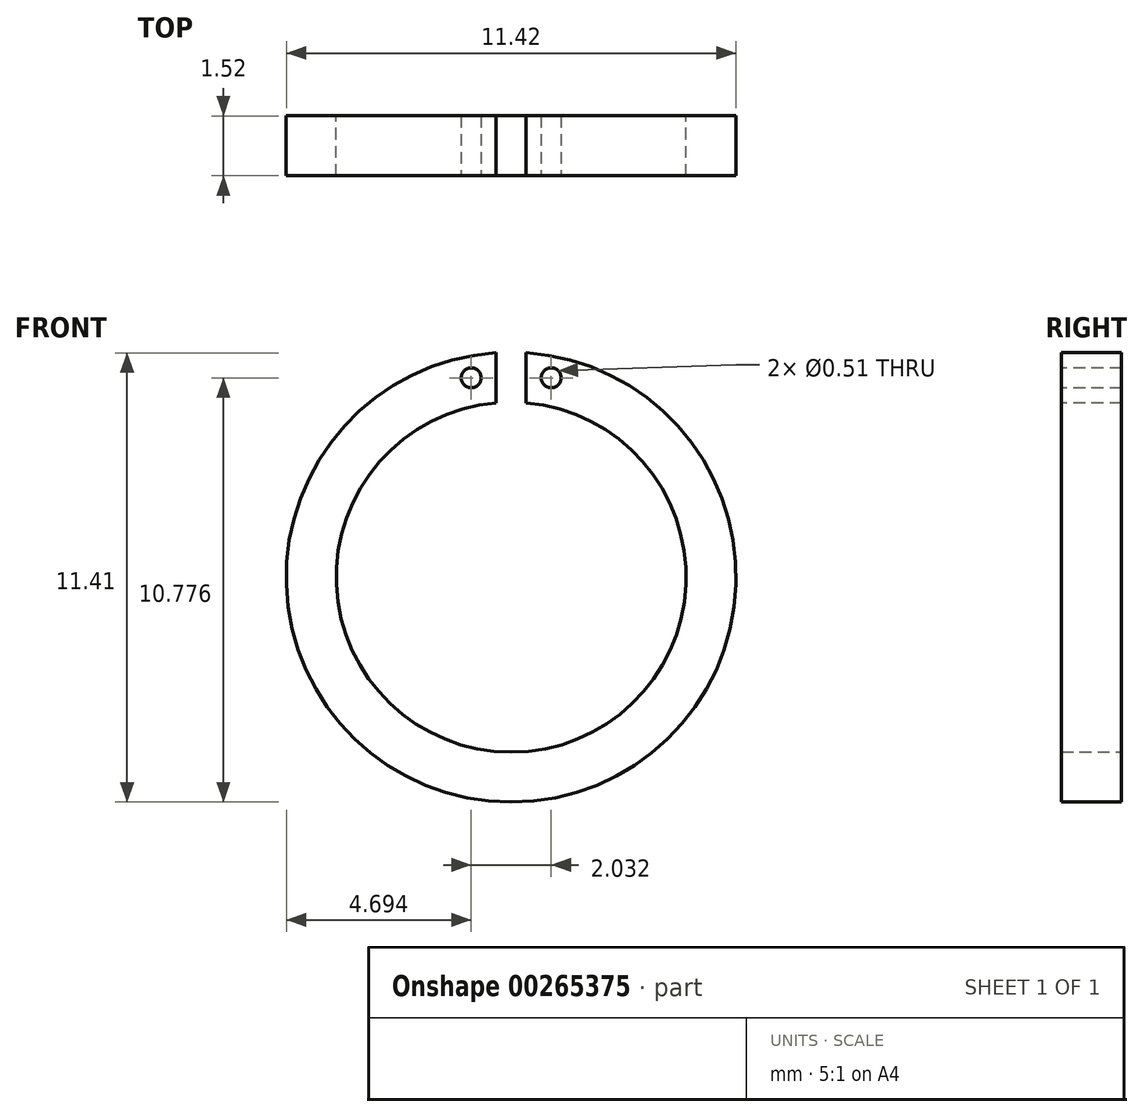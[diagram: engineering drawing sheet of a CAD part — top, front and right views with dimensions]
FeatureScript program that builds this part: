
annotation { "Feature Type Name" : "Feature", "Feature Type Description" : "" }
export const myFeature = defineFeature(function(context is Context, id is Id, definition is map)
    precondition{}
    {
        {
            var Q0;
            Q0=qCreatedBy(makeId("Front.planeOp"),FACE);
            var sketch = newSketch(context, id + "F0", { "sketchPlane" : qUnion([Q0])});
            skCircle(sketch, "E0", {"center": v(0, 0) * mm, "radius": 4.45 * mm});
            skCircle(sketch, "E1", {"center": v(0, 0) * mm, "radius": 5.72 * mm});
            skSolve(sketch);
        }
        {
            var Q0;
            Q0 = qSketchRegion(id + "F0", true);
            extrude(context, id + "F1", {"entities" : qUnion([Q0]), "depth" : 1.52 * mm, "symmetric" : true});
        }
        {
            var Q0;
            Q0=qCreatedBy(makeId("Front.planeOp"),FACE);
            var sketch = newSketch(context, id + "F2", { "sketchPlane" : qUnion([Q0])});
            skLineSegment(sketch, "E2", {"start": v(-0.38, 5.7) * mm, "end": v(-0.38, 4.43) * mm});
            skLineSegment(sketch, "E3", {"start": v(0.38, 5.7) * mm, "end": v(0.38, 4.43) * mm});
            skArc(sketch, "E4.0", {"start": v(0.38, 5.7) * mm, "mid": v(0, 5.72) * mm, "end": v(-0.38, 5.7) * mm});
            skArc(sketch, "E5.0", {"start": v(0.38, 4.43) * mm, "mid": v(0, 4.45) * mm, "end": v(-0.38, 4.43) * mm});
            skCircle(sketch, "E6", {"center": v(1.02, 5.07) * mm, "radius": 0.25 * mm});
            skPoint(sketch, "E6.centerSnap0", {"position": v(0.38, 5.07) * mm});
            skCircle(sketch, "E7", {"center": v(-1.02, 5.07) * mm, "radius": 0.25 * mm});
            skPoint(sketch, "E7.centerSnap0", {"position": v(-0.38, 5.07) * mm});
            skSolve(sketch);
        }
        {
            var Q0;
            Q0 = qSketchRegion(id + "F2", true);
            extrude(context, id + "F3", {"entities" : qUnion([Q0]), "operationType" : NewBodyOperationType.REMOVE, "oppositeDirection" : true, "depth" : 25.4 * mm, "symmetric" : true});
        }
    });
